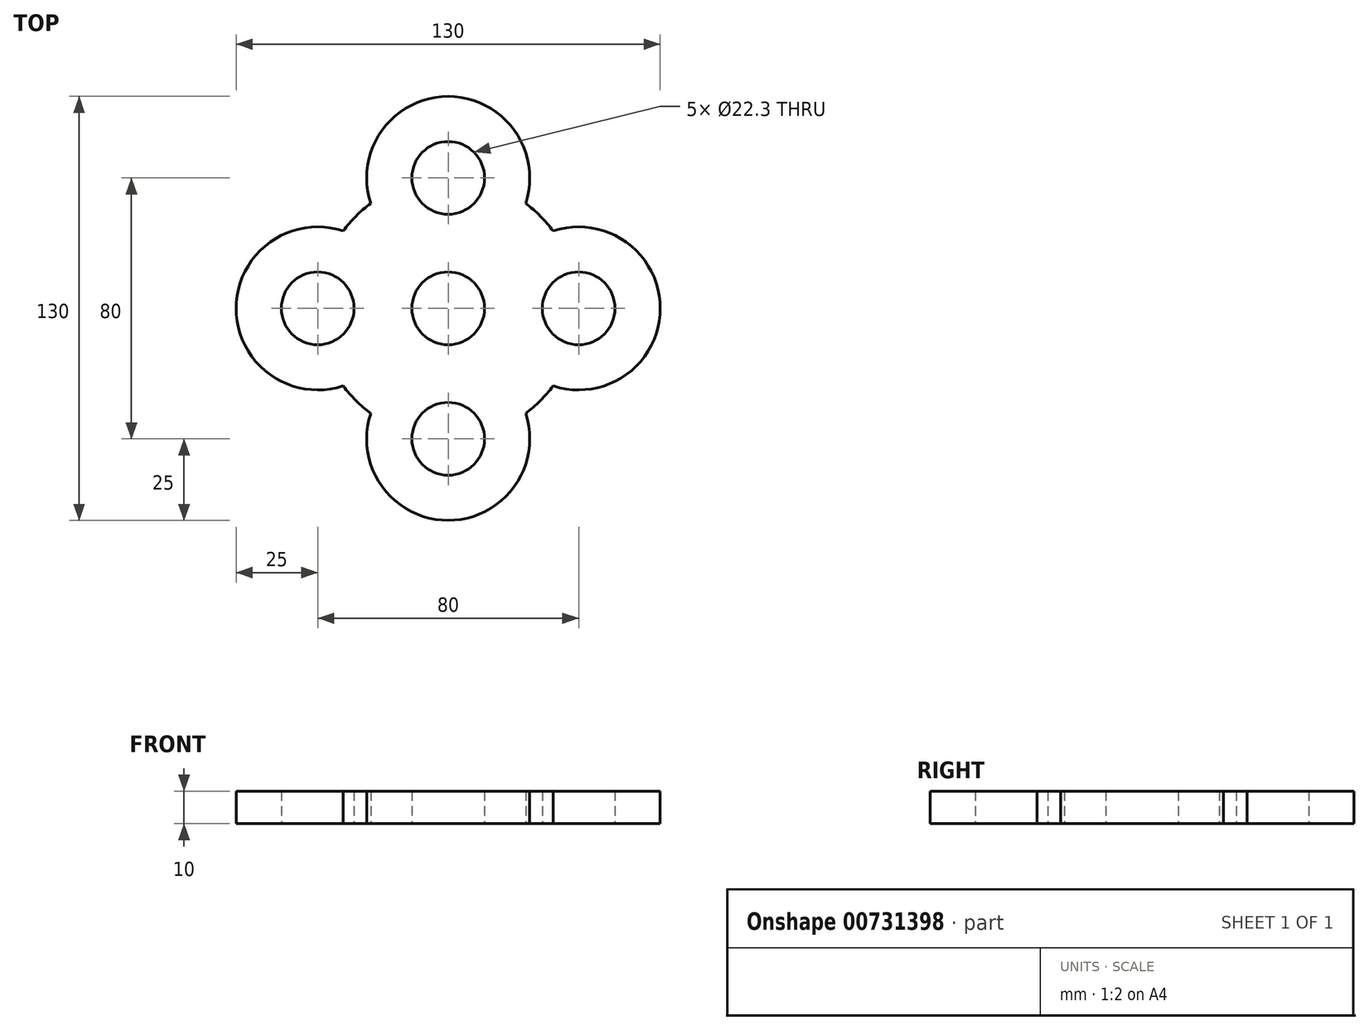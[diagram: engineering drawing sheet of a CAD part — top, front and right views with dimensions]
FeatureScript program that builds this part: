
annotation { "Feature Type Name" : "Feature", "Feature Type Description" : "" }
export const myFeature = defineFeature(function(context is Context, id is Id, definition is map)
    precondition{}
    {
        {
            var Q0;
            Q0=qCreatedBy(makeId("Top.planeOp"),FACE);
            var sketch = newSketch(context, id + "F0", { "sketchPlane" : qUnion([Q0])});
            skCircle(sketch, "E0", {"center": v(0, 0) * mm, "radius": 40 * mm});
            skCircle(sketch, "E1", {"center": v(0, 40) * mm, "radius": 25 * mm});
            skCircle(sketch, "E2", {"center": v(40, 0) * mm, "radius": 25 * mm});
            skCircle(sketch, "E3", {"center": v(0, -40) * mm, "radius": 25 * mm});
            skCircle(sketch, "E4", {"center": v(-40, 0) * mm, "radius": 25 * mm});
            skCircle(sketch, "E5", {"center": v(0, 0) * mm, "radius": 11.15 * mm});
            skCircle(sketch, "E6", {"center": v(40, 0) * mm, "radius": 11.15 * mm});
            skCircle(sketch, "E7", {"center": v(-40, 0) * mm, "radius": 11.15 * mm});
            skCircle(sketch, "E8", {"center": v(0, 40) * mm, "radius": 11.15 * mm});
            skCircle(sketch, "E9", {"center": v(0, -40) * mm, "radius": 11.15 * mm});
            skSolve(sketch);
        }
        {
            var Q0;
            Q0 = qSketchRegion(id + "F0", true);
            extrude(context, id + "F1", {"entities" : qUnion([Q0]), "depth" : 10 * mm, "offsetDistance" : 25 * mm});
        }
    });
